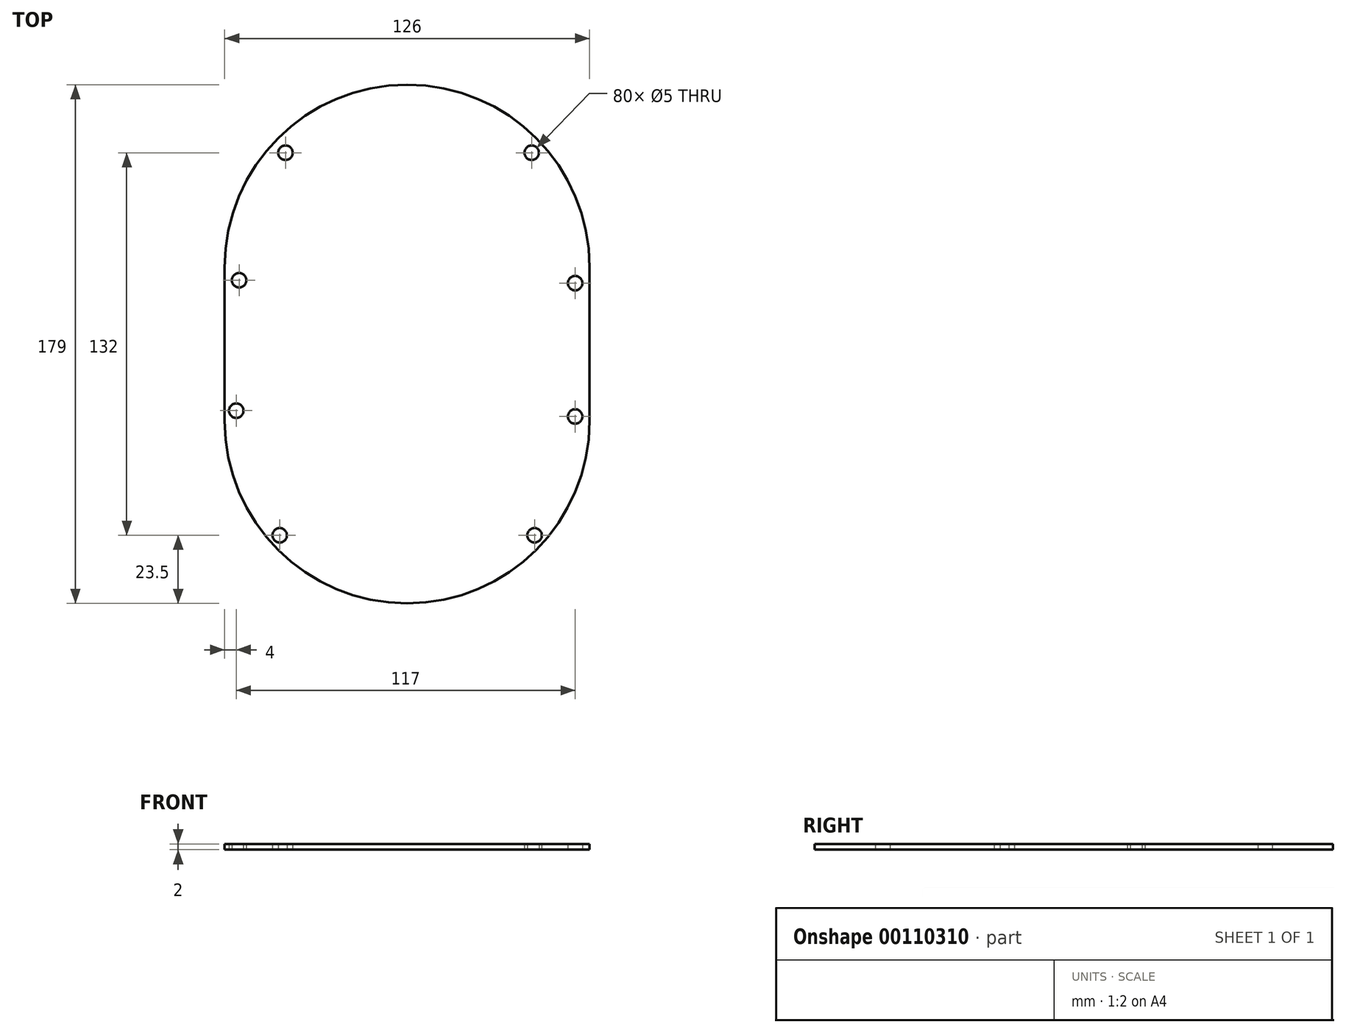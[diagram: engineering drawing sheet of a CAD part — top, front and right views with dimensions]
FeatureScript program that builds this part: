
annotation { "Feature Type Name" : "Feature", "Feature Type Description" : "" }
export const myFeature = defineFeature(function(context is Context, id is Id, definition is map)
    precondition{}
    {
        {
            var Q0;
            Q0=qCreatedBy(makeId("Top.planeOp"),FACE);
            var sketch = newSketch(context, id + "F0", { "sketchPlane" : qUnion([Q0])});
            skLineSegment(sketch, "E0", {"start": v(0, 0) * mm, "end": v(0, 53) * mm});
            skArc(sketch, "E1.0.startCap", {"start": v(50, 0) * mm, "mid": v(0, -50) * mm, "end": v(-50, 0) * mm});
            skArc(sketch, "E1.0.endCap", {"start": v(-50, 53) * mm, "mid": v(0, 103) * mm, "end": v(50, 53) * mm});
            skLineSegment(sketch, "E1.0.left", {"start": v(-50, 0) * mm, "end": v(-50, 53) * mm});
            skLineSegment(sketch, "E1.0.right", {"start": v(50, 0) * mm, "end": v(50, 53) * mm});
            skLineSegment(sketch, "E2.0", {"start": v(-63, 0) * mm, "end": v(-63, 53) * mm});
            skArc(sketch, "E2.1", {"start": v(63, 0) * mm, "mid": v(0, -63) * mm, "end": v(-63, 0) * mm});
            skLineSegment(sketch, "E2.2", {"start": v(63, 0) * mm, "end": v(63, 53) * mm});
            skArc(sketch, "E2.3", {"start": v(-63, 53) * mm, "mid": v(0, 116) * mm, "end": v(63, 53) * mm});
            skLineSegment(sketch, "E3", {"start": v(0, 26.5) * mm, "end": v(-117.83, 26.5) * mm});
            skLineSegment(sketch, "E4", {"start": v(-117.83, 26.5) * mm, "end": v(106.92, 26.5) * mm, "construction": true});
            skPoint(sketch, "E5.startSnap0", {"position": v(0, -63) * mm});
            skCircle(sketch, "E6", {"center": v(58, 47.5) * mm, "radius": 2.5 * mm});
            skCircle(sketch, "E7", {"center": v(43, 92.5) * mm, "radius": 2.5 * mm});
            skCircle(sketch, "E8.MirrorC", {"center": v(58, 1.5) * mm, "radius": 2.5 * mm});
            skCircle(sketch, "E9.MirrorC", {"center": v(44, -39.5) * mm, "radius": 2.5 * mm});
            skCircle(sketch, "E10", {"center": v(-44, -39.5) * mm, "radius": 2.5 * mm});
            skCircle(sketch, "E11", {"center": v(-59, 3.5) * mm, "radius": 2.5 * mm});
            skCircle(sketch, "E12", {"center": v(-42, 92.5) * mm, "radius": 2.5 * mm});
            skCircle(sketch, "E13", {"center": v(-58, 48.5) * mm, "radius": 2.5 * mm});
            skLineSegment(sketch, "E14", {"start": v(0, 116) * mm, "end": v(0, -50) * mm, "construction": true});
            skSolve(sketch);
        }
        {
            var Q0;
            Q0 = qSketchRegion(id + "F0", true);
            var Q1;
            Q1=makeQuery(id+"F0.imprint","IMPRINT",FACE,{"disambiguationData":[TD([[makeQuery(id+"F0.imprint","IMPRINT",EDGE,{"derivedFrom":sQuery(id+"F0.wireOp",EDGE,"E1.0.startCap")}),1.0]])]});
            extrude(context, id + "F1", {"entities" : qUnion([Q0, Q1]), "depth" : 2 * mm});
        }
    });
